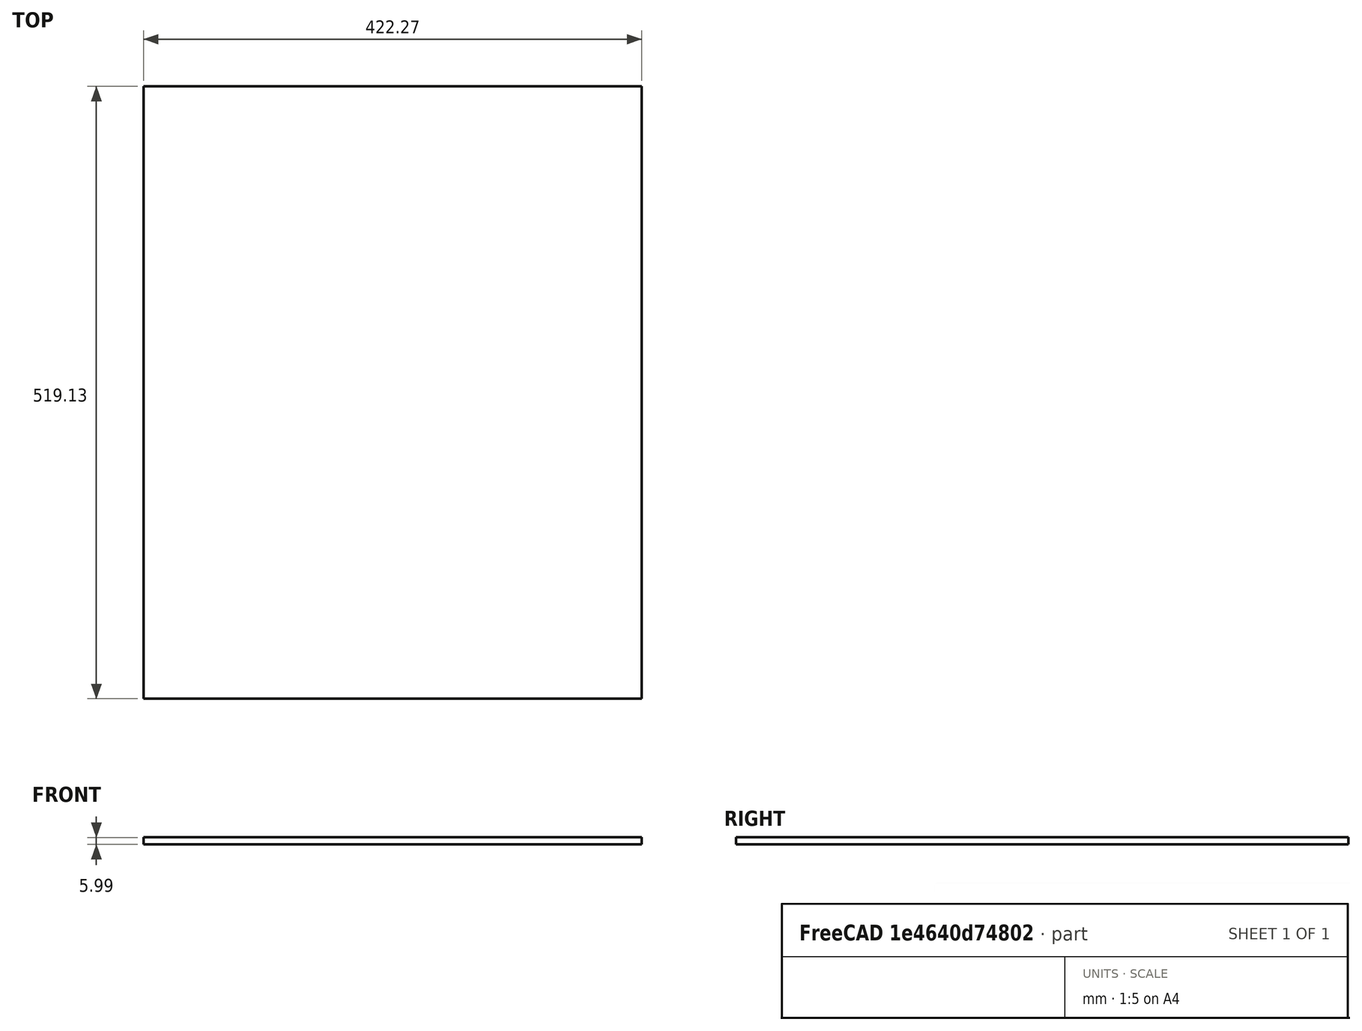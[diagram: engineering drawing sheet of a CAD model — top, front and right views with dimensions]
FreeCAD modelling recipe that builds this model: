
FCSTD DOCUMENT  (FreeCAD 0.19R24267 (Git))
Label: Up1-P6
License: All rights reserved
LicenseURL: http://en.wikipedia.org/wiki/All_rights_reserved
objects: TechDraw::DrawViewDimension×3, TechDraw::DrawProjGroupItem×2, TechDraw::DrawHatch×2, TechDraw::DrawViewAnnotation×2, Sketcher::SketchObject×1, Part::Extrusion×1, TechDraw::DrawSVGTemplate×1, TechDraw::DrawProjGroup×1, TechDraw::DrawPage×1
note: 2 computed .brp shape members not serialized (recipe doc carries the construction recipe); baked Part::Feature solids carry a one-line shape summary decoded from their .brp

FEATURE [Sketcher::SketchObject] Sketch
  FullyConstrained = false
  sketch-geometry (4):
    g0: LineSegment StartX=0 StartY=0 StartZ=0 EndX=422.275 EndY=0 EndZ=0
    g1: LineSegment StartX=422.275 StartY=0 StartZ=0 EndX=422.275 EndY=519.125 EndZ=0
    g2: LineSegment StartX=422.275 StartY=519.125 StartZ=0 EndX=0 EndY=519.125 EndZ=0
    g3: LineSegment StartX=0 StartY=519.125 StartZ=0 EndX=0 EndY=0 EndZ=0
  constraints (11):
    c: Coincident(g0,g1)
    c: Coincident(g1,g2)
    c: Coincident(g2,g3)
    c: Coincident(g3,g0)
    c: Horizontal(g0)
    c: Horizontal(g2)
    c: Vertical(g1)
    c: Vertical(g3)
    c: Coincident(g0,g-1)
    c: DistanceX(g2,g2) = 422.275
    c: DistanceY(g3,g3) = 519.125
FEATURE [Part::Extrusion] Extrude
  Base = -> Sketch
  Dir = (0,0,1)
  DirMode = 2
  FaceMakerClass = Part::FaceMakerBullseye
  LengthFwd = 5.9944
  LengthRev = 0
  Solid = true
  Symmetric = false
FEATURE [TechDraw::DrawSVGTemplate] Template
  Height = 215.9
  Orientation = 1
  Width = 279.4
FEATURE [TechDraw::DrawProjGroupItem] ProjItem  label="Front"
  CoarseView = false
  Direction = (0,0,1)
  Focus = 100
  HardHidden = false
  IsoCount = 0
  IsoHidden = false
  IsoVisible = false
  LockPosition = true
  Perspective = false
  Rotation = 0
  RotationVector = (-1,0,0)
  Scale = 0.25
  ScaleType = 2
  SeamHidden = false
  SeamVisible = true
  SmoothHidden = false
  SmoothVisible = true
  Source = -> [Extrude]
  Type = 0
  X = 0
  XDirection = (-1,0,0)
  Y = 0
FEATURE [TechDraw::DrawProjGroupItem] ProjItem001  label="Left"
  CoarseView = false
  Direction = (1,0,1e-16)
  Focus = 100
  HardHidden = false
  IsoCount = 0
  IsoHidden = false
  IsoVisible = false
  LockPosition = false
  Perspective = false
  Rotation = 0
  RotationVector = (1,0,0)
  ScaleType = 2
  SeamHidden = false
  SeamVisible = true
  SmoothHidden = false
  SmoothVisible = true
  Source = -> [Extrude]
  Type = 1
  X = 83.4355
  XDirection = (-1e-16,0,1)
  Y = 0
FEATURE [TechDraw::DrawProjGroup] ProjGroup
  Anchor = -> ProjItem
  AutoDistribute = true
  LockPosition = false
  ProjectionType = 0
  Rotation = 0
  Scale = 0.25
  ScaleType = 2
  Source = -> [Extrude]
  Views = -> [ProjItem,ProjItem001]
  X = 139.7
  Y = 107.95
  spacingX = 15.0114
  spacingY = 15.0114
FEATURE [TechDraw::DrawHatch] Hatch  label="HatchF0"
  HatchPattern = <path>
  Source = -> ProjItem [Face0]
FEATURE [TechDraw::DrawHatch] Hatch001  label="Hatch001F0"
  HatchPattern = <path>
  Source = -> ProjItem001 [Face0]
FEATURE [TechDraw::DrawViewDimension] Dimension
  Arbitrary = false
  ArbitraryTolerances = false
  EqualTolerance = true
  FormatSpec = %.3f
  FormatSpecOverTolerance = %+.3f
  FormatSpecUnderTolerance = %+.3f
  Inverted = false
  LockPosition = false
  MeasureType = 1
  OverTolerance = 0
  References2D = -> [ProjItem]
  Rotation = 0
  ScaleType = 0
  TheoreticalExact = false
  Type = 2
  UnderTolerance = 0
  X = 60.4469
  Y = 0.613004
FEATURE [TechDraw::DrawViewDimension] Dimension001
  Arbitrary = false
  ArbitraryTolerances = false
  EqualTolerance = true
  FormatSpec = %.3f
  FormatSpecOverTolerance = %+.3f
  FormatSpecUnderTolerance = %+.3f
  Inverted = false
  LockPosition = false
  MeasureType = 1
  OverTolerance = 0
  References2D = -> [ProjItem]
  Rotation = 0
  ScaleType = 0
  TheoreticalExact = false
  Type = 1
  UnderTolerance = 0
  X = -0.613004
  Y = -72.2467
FEATURE [TechDraw::DrawViewDimension] Dimension002
  Arbitrary = false
  ArbitraryTolerances = false
  EqualTolerance = true
  FormatSpec = %.3f
  FormatSpecOverTolerance = %+.3f
  FormatSpecUnderTolerance = %+.3f
  Inverted = false
  LockPosition = false
  MeasureType = 1
  OverTolerance = 0
  References2D = -> [ProjItem001]
  Rotation = 0
  ScaleType = 0
  TheoreticalExact = false
  Type = 1
  UnderTolerance = 0
  X = 14.7302
  Y = 54.096
FEATURE [TechDraw::DrawViewAnnotation] Annotation
  Font = osifont
  LineSpace = 80
  LockPosition = false
  MaxWidth = -1
  Rotation = 0
  ScaleType = 0
  Text = Figure S3 (Upright) | Panel 6 [back right] | Quantity: 1
  TextSize = 5.0038
  TextStyle = 0
  X = 30.4437
  Y = 195.58
FEATURE [TechDraw::DrawViewAnnotation] Annotation001
  Font = osifont
  LineSpace = 80
  LockPosition = false
  MaxWidth = -1
  Rotation = 0
  ScaleType = 0
  Text = Units: Inches
  TextSize = 5.0038
  TextStyle = 0
  X = 259.08
  Y = 5.08
FEATURE [TechDraw::DrawPage] Page
  KeepUpdated = true
  NextBalloonIndex = 1
  ProjectionType = 0
  Template = -> Template
  Views = -> [ProjGroup,Dimension,Dimension001,Dimension002,Annotation,Annotation001]
note: 2 file-system paths scrubbed to <path> (originals preserved in the JSON sidecar)
